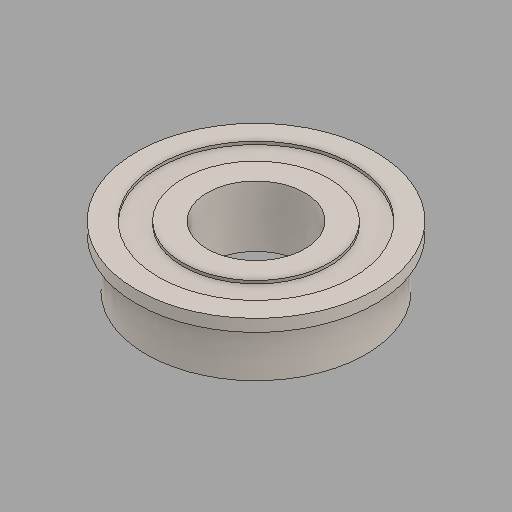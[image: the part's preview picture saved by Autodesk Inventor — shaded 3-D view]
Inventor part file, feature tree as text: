
AUTODESK INVENTOR PART (.ipt)
format: ipt  version: 2024.2 (Build 282272000, 272)  size: 123,392 bytes
history: native  units: in
note: dims shown in document units (in); Inventor stores cm internally (conversion verified against a paired STEP export)
features: revolve x1
ambient origin geometry x8: Origin, YZ Plane, XZ Plane, XY Plane, X Axis, Y Axis, Z Axis, Center Point
bodies: Solid1 (feature_tree)
feature tree (1):
  revolve  "Revolve1"  [1 undecoded]
note: 1 required parameter value undecoded (feature->parameter linkage not recoverable at this tier; creation-order binding heuristic only, values carry confidence <= 0.55)
